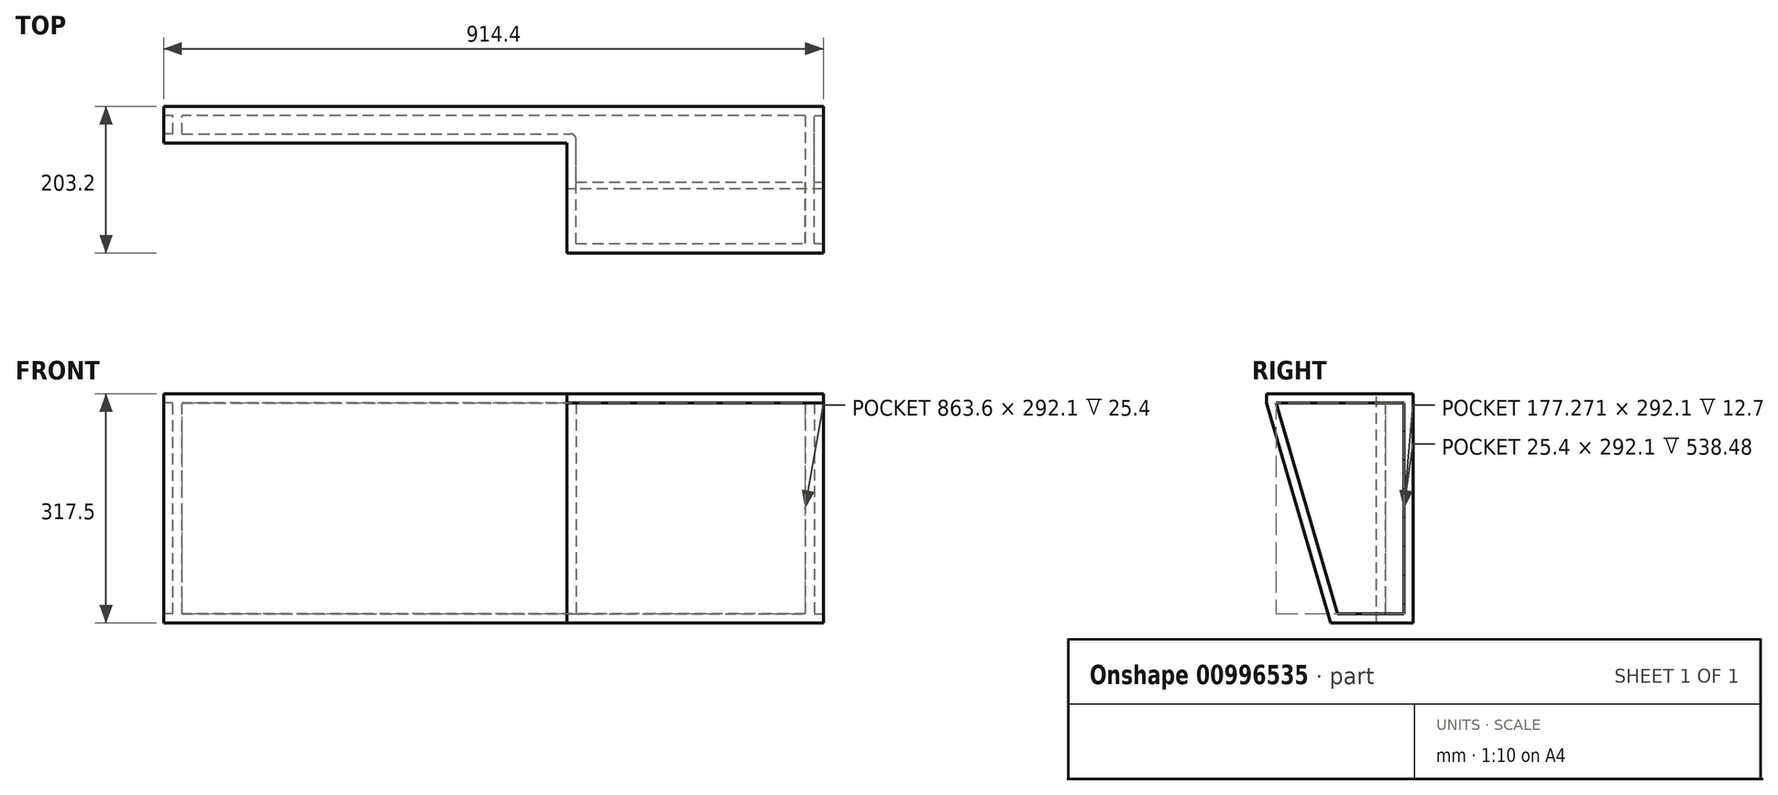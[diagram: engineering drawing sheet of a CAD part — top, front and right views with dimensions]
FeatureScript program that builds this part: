
annotation { "Feature Type Name" : "Feature", "Feature Type Description" : "" }
export const myFeature = defineFeature(function(context is Context, id is Id, definition is map)
    precondition{}
    {
        {
            var Q0;
            Q0=qCreatedBy(makeId("Front.planeOp"),FACE);
            var sketch = newSketch(context, id + "F0", { "sketchPlane" : qUnion([Q0])});
            skLineSegment(sketch, "E0.bottom", {"start": v(177.8, 158.75) * mm, "end": v(-177.8, 158.75) * mm});
            skLineSegment(sketch, "E0.top", {"start": v(177.8, -158.75) * mm, "end": v(-177.8, -158.75) * mm});
            skLineSegment(sketch, "E0.left", {"start": v(177.8, 158.75) * mm, "end": v(177.8, -158.75) * mm});
            skLineSegment(sketch, "E0.right", {"start": v(-177.8, 158.75) * mm, "end": v(-177.8, -158.75) * mm});
            skPoint(sketch, "E0.middle", {"position": v(0, 0) * mm});
            skSolve(sketch);
        }
        {
            var Q0;
            Q0=makeQuery(id+"F0.imprint","IMPRINT",FACE,{"disambiguationData":[TD([[makeQuery(id+"F0.imprint","IMPRINT",EDGE,{"derivedFrom":sQuery(id+"F0.wireOp",EDGE,"E0.bottom")}),1.0]])]});
            extrude(context, id + "F1", {"entities" : qUnion([Q0]), "depth" : 203.2 * mm, "offsetDistance" : 25.4 * mm});
        }
        {
            var Q0;
            Q0=makeQuery(id+"F1.opExtrude","SWEPT_FACE",FACE,{"disambiguationData":[OSD([sQuery(id+"F0.wireOp",EDGE,"E0.bottom")])]});
            var sketch = newSketch(context, id + "F2", { "sketchPlane" : qUnion([Q0])});
            skSolve(sketch);
        }
        {
            var Q0;
            Q0=makeQuery(id+"F1.opExtrude","CAP_EDGE",EDGE,{"disambiguationData":[OSD([sQuery(id+"F0.wireOp",EDGE,"E0.top")])],"isStart":false});
            chamfer(context, id + "F3", {"entities" : qUnion([Q0]), "chamferType" : ChamferType.TWO_OFFSETS, "width1" : 88.9 * mm, "oppositeDirection" : false, "width2" : 304.8 * mm, "tangentPropagation" : true});
        }
        {
            var Q0;
            Q0=makeQuery(id+"F1.opExtrude","SWEPT_FACE",FACE,{"disambiguationData":[OSD([sQuery(id+"F0.wireOp",EDGE,"E0.right")])]});
            var sketch = newSketch(context, id + "F4", { "sketchPlane" : qUnion([Q0])});
            skLineSegment(sketch, "E1.0", {"start": v(0, 158.75) * mm, "end": v(0, -158.75) * mm});
            skLineSegment(sketch, "E2.bottom", {"start": v(0, -158.75) * mm, "end": v(50.8, -158.75) * mm});
            skLineSegment(sketch, "E2.top", {"start": v(0, 158.75) * mm, "end": v(50.8, 158.75) * mm});
            skLineSegment(sketch, "E2.left", {"start": v(0, -158.75) * mm, "end": v(0, 158.75) * mm});
            skLineSegment(sketch, "E2.right", {"start": v(50.8, -158.75) * mm, "end": v(50.8, 158.75) * mm});
            skSolve(sketch);
        }
        {
            var Q0;
            Q0=makeQuery(id+"F4.imprint","IMPRINT",FACE,{"disambiguationData":[TD([[makeQuery(id+"F4.imprint","IMPRINT",EDGE,{"derivedFrom":sQuery(id+"F4.wireOp",EDGE,"E2.bottom")}),-1.0]])]});
            extrude(context, id + "F5", {"entities" : qUnion([Q0]), "operationType" : NewBodyOperationType.ADD, "depth" : 558.8 * mm, "offsetDistance" : 25.4 * mm});
        }
        {
            var Q0;
            Q0=makeQuery(id+"F1.opExtrude","SWEPT_FACE",FACE,{"disambiguationData":[OSD([sQuery(id+"F0.wireOp",EDGE,"E0.left")])]});
            var sketch = newSketch(context, id + "F6", { "sketchPlane" : qUnion([Q0])});
            skLineSegment(sketch, "E3.0", {"start": v(-206.9, 158.75) * mm, "end": v(0, 158.75) * mm});
            skLineSegment(sketch, "E4.0", {"start": v(0, 158.75) * mm, "end": v(0, -158.75) * mm});
            skLineSegment(sketch, "E5.0", {"start": v(-206.9, 158.75) * mm, "end": v(-114.3, -158.75) * mm});
            skPoint(sketch, "E6.0", {"position": v(-50.8, -158.75) * mm});
            skLineSegment(sketch, "E7.0", {"start": v(-114.3, -158.75) * mm, "end": v(0, -158.75) * mm});
            skLineSegment(sketch, "E8.0", {"start": v(-189.97, 146.05) * mm, "end": v(-104.77, -146.05) * mm});
            skLineSegment(sketch, "E8.1", {"start": v(-189.97, 146.05) * mm, "end": v(-12.7, 146.05) * mm});
            skLineSegment(sketch, "E8.2", {"start": v(-12.7, 146.05) * mm, "end": v(-12.7, -146.05) * mm});
            skLineSegment(sketch, "E8.3", {"start": v(-104.78, -146.05) * mm, "end": v(-12.7, -146.05) * mm});
            skSolve(sketch);
        }
        {
            var Q0;
            Q0=makeQuery(id+"F6.imprint","IMPRINT",FACE,{"disambiguationData":[TD([[makeQuery(id+"F6.imprint","IMPRINT",EDGE,{"derivedFrom":sQuery(id+"F6.wireOp",EDGE,"E8.0")}),1.0]])]});
            extrude(context, id + "F7", {"entities" : qUnion([Q0]), "operationType" : NewBodyOperationType.REMOVE, "oppositeDirection" : true, "depth" : 12.7 * mm, "offsetDistance" : 25.4 * mm});
        }
        {
            var Q0;
            Q0=makeQuery(id+"F5.opExtrude","CAP_FACE",FACE,{"disambiguationData":[OSD([sQuery(id+"F4.wireOp",EDGE,"E2.bottom"),sQuery(id+"F4.wireOp",EDGE,"E2.top"),sQuery(id+"F4.wireOp",EDGE,"E2.left"),sQuery(id+"F4.wireOp",EDGE,"E2.right")])],"isStart":false});
            var sketch = newSketch(context, id + "F8", { "sketchPlane" : qUnion([Q0])});
            skLineSegment(sketch, "E9.0", {"start": v(38.1, -146.05) * mm, "end": v(38.1, 146.05) * mm});
            skLineSegment(sketch, "E9.1", {"start": v(38.1, -146.05) * mm, "end": v(12.7, -146.05) * mm});
            skLineSegment(sketch, "E9.2", {"start": v(12.7, 146.05) * mm, "end": v(12.7, -146.05) * mm});
            skLineSegment(sketch, "E9.3", {"start": v(38.1, 146.05) * mm, "end": v(12.7, 146.05) * mm});
            skSolve(sketch);
        }
        {
            var Q0;
            Q0=makeQuery(id+"F8.imprint","IMPRINT",FACE,{"disambiguationData":[TD([[makeQuery(id+"F8.imprint","IMPRINT",EDGE,{"derivedFrom":sQuery(id+"F8.wireOp",EDGE,"E9.0")}),1.0]])]});
            extrude(context, id + "F9", {"entities" : qUnion([Q0]), "operationType" : NewBodyOperationType.REMOVE, "oppositeDirection" : true, "depth" : 12.7 * mm, "offsetDistance" : 25.4 * mm});
        }
        {
            var Q0;
            Q0=makeQuery(id+"F5.boolean.opBoolean","MERGE",FACE,{"derivedFrom":[makeQuery(id+"F1.opExtrude","SWEPT_FACE",FACE,{"disambiguationData":[OSD([sQuery(id+"F0.wireOp",EDGE,"E0.bottom")])]}),makeQuery(id+"F5.opExtrude","SWEPT_FACE",FACE,{"disambiguationData":[OSD([sQuery(id+"F4.wireOp",EDGE,"E2.top")])]})]});
            var Q1;
            Q1=makeQuery(id+"F1.opExtrude","SWEPT_BODY",BODY,{"disambiguationData":[OSD([sQuery(id+"F0.wireOp",EDGE,"E0.bottom"),sQuery(id+"F0.wireOp",EDGE,"E0.top"),sQuery(id+"F0.wireOp",EDGE,"E0.left"),sQuery(id+"F0.wireOp",EDGE,"E0.right")])]});
            shell(context, id + "F10", {"isHollow" : true, "entities" : qUnion([Q0]), "parts" : qUnion([Q1]), "thickness" : 12.7 * mm});
        }
        {
            var Q0;
            Q0=makeQuery(id+"F3.opChamfer","BLEND_FACE",FACE,{"disambiguationData":[OSD([sQuery(id+"F0.wireOp",EDGE,"E0.top")])]});
            var sketch = newSketch(context, id + "F11", { "sketchPlane" : qUnion([Q0])});
            skCircle(sketch, "E10", {"center": v(0, 0) * mm, "radius": 90.49 * mm});
            skSolve(sketch);
        }
        {
            var Q0;
            {var subQ0=sQuery(id+"F4.wireOp",EDGE,"E2.right");Q0=makeQuery(id+"F4.imprint","IMPRINT",FACE,{"disambiguationData":[TD([[makeQuery(id+"F4.imprint","IMPRINT",EDGE,{"derivedFrom":subQ0}),-1.0]])]});}
            var sketch = newSketch(context, id + "F12", { "sketchPlane" : qUnion([Q0])});
            skLineSegment(sketch, "E11.0", {"start": v(114.3, -158.75) * mm, "end": v(50.8, -158.75) * mm});
            skLineSegment(sketch, "E12.0", {"start": v(114.3, -158.75) * mm, "end": v(206.9, 158.75) * mm});
            skLineSegment(sketch, "E13.0", {"start": v(206.9, 158.75) * mm, "end": v(50.8, 158.75) * mm});
            skPoint(sketch, "E14.0", {"position": v(0, 158.75) * mm});
            skLineSegment(sketch, "E15.0.0", {"start": v(50.8, -158.75) * mm, "end": v(50.8, 158.75) * mm});
            skLineSegment(sketch, "E15.0.2", {"start": v(50.8, 158.75) * mm, "end": v(50.8, -158.75) * mm});
            skLineSegment(sketch, "E16.0", {"start": v(189.97, 146.05) * mm, "end": v(50.8, 146.05) * mm});
            skLineSegment(sketch, "E16.1", {"start": v(104.78, -146.05) * mm, "end": v(189.97, 146.05) * mm});
            skLineSegment(sketch, "E16.2", {"start": v(104.78, -146.05) * mm, "end": v(50.8, -146.05) * mm});
            skSolve(sketch);
        }
        {
            var Q0;
            Q0=makeQuery(id+"F10.opShell","OFFSET_EDGE",EDGE,{"disambiguationData":[OSD([sQuery(id+"F4.wireOp",EDGE,"E2.right")])]});
            fillet(context, id + "F13", {"entities" : qUnion([Q0]), "radius" : 7.62 * mm, "tangentPropagation" : true, "allowEdgeOverflow" : false});
        }
    });
